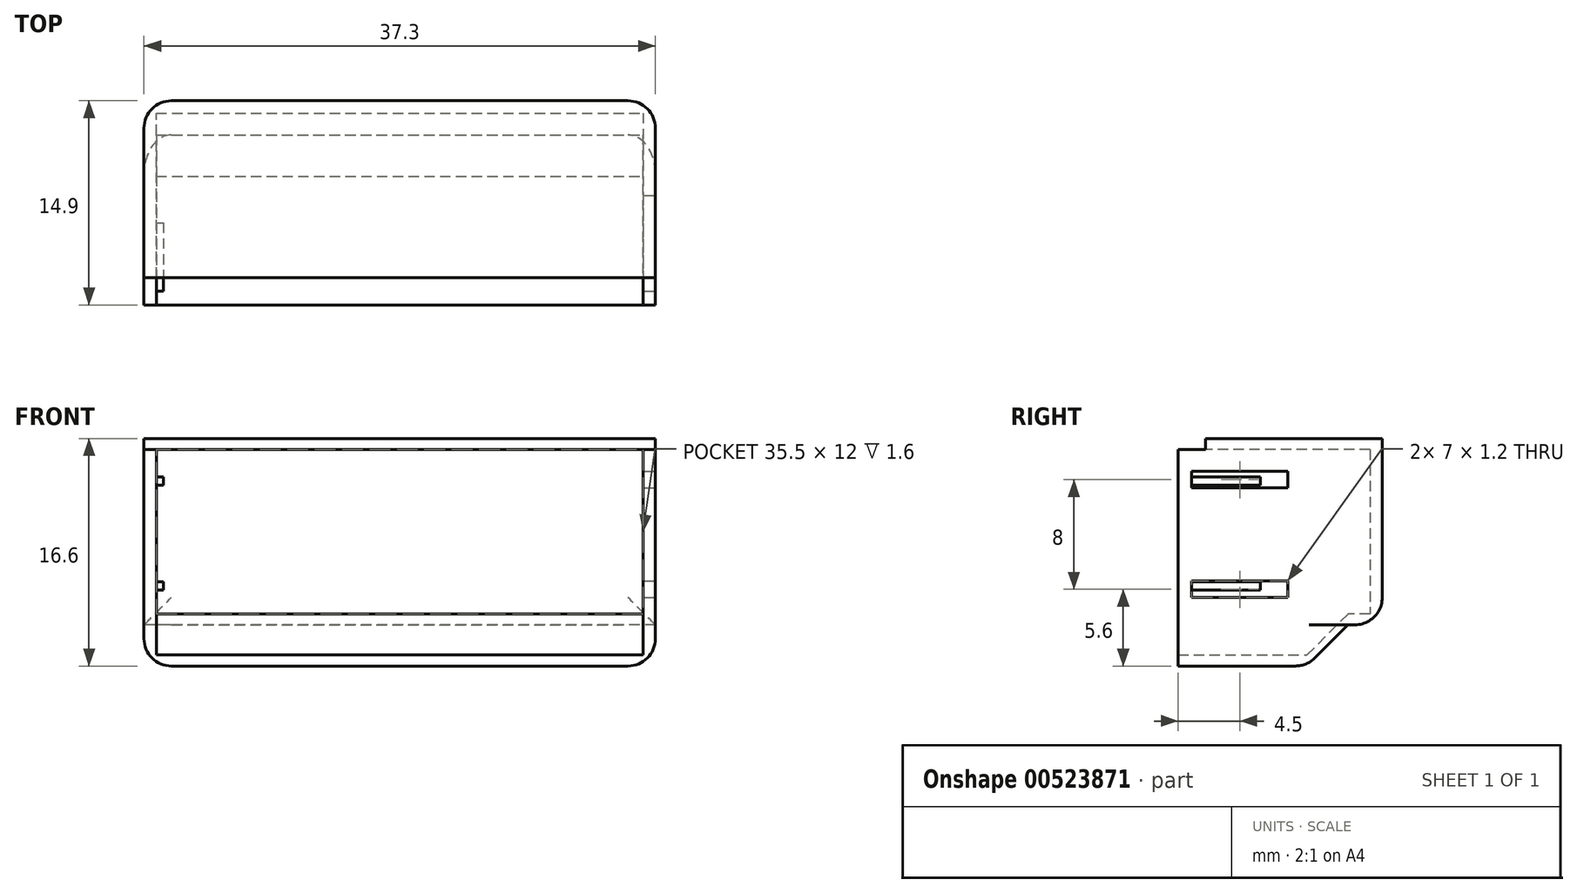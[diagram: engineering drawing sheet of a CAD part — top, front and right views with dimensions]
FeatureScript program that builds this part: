
annotation { "Feature Type Name" : "Feature", "Feature Type Description" : "" }
export const myFeature = defineFeature(function(context is Context, id is Id, definition is map)
    precondition{}
    {
        {
            var Q0;
            Q0=qCreatedBy(makeId("Top.planeOp"),FACE);
            var sketch = newSketch(context, id + "F0", { "sketchPlane" : qUnion([Q0])});
            skLineSegment(sketch, "E0", {"start": v(0, 0) * mm, "end": v(0, 14) * mm});
            skLineSegment(sketch, "E1", {"start": v(0, 14) * mm, "end": v(35.5, 14) * mm});
            skLineSegment(sketch, "E2", {"start": v(35.5, 14) * mm, "end": v(35.5, 0) * mm});
            skLineSegment(sketch, "E3.0", {"start": v(36.4, 14.9) * mm, "end": v(36.4, 0) * mm});
            skLineSegment(sketch, "E3.1", {"start": v(-0.9, 14.9) * mm, "end": v(36.4, 14.9) * mm});
            skLineSegment(sketch, "E3.2", {"start": v(-0.9, 0) * mm, "end": v(-0.9, 14.9) * mm});
            skLineSegment(sketch, "E4", {"start": v(-0.9, 0) * mm, "end": v(0, 0) * mm});
            skLineSegment(sketch, "E5", {"start": v(35.5, 0) * mm, "end": v(36.4, 0) * mm});
            skSolve(sketch);
        }
        {
            var Q0;
            Q0 = qSketchRegion(id + "F0", true);
            extrude(context, id + "F1", {"entities" : qUnion([Q0]), "depth" : 17 * mm, "offsetDistance" : 25 * mm});
        }
        {
            var Q0;
            Q0=makeQuery(id+"F1.opExtrude","SWEPT_FACE",FACE,{"disambiguationData":[OSD([sQuery(id+"F0.wireOp",EDGE,"E4")])]});
            cPlane(context, id + "F2", {"entities" : qUnion([Q0]), "cplaneType" : CPlaneType.OFFSET, "offset" : 1 * mm, "oppositeDirection" : true, "width" : 150 * mm, "height" : 150 * mm});
        }
        {
            var Q0;
            Q0=qCreatedBy(id+"F2.planeOp",FACE);
            var sketch = newSketch(context, id + "F3", { "sketchPlane" : qUnion([Q0])});
            skLineSegment(sketch, "E6.bottom", {"start": v(0, 15) * mm, "end": v(0.5, 15) * mm});
            skLineSegment(sketch, "E6.top", {"start": v(0, 14.4) * mm, "end": v(0.5, 14.4) * mm});
            skLineSegment(sketch, "E6.left", {"start": v(0, 15) * mm, "end": v(0, 14.4) * mm});
            skLineSegment(sketch, "E6.right", {"start": v(0.5, 15) * mm, "end": v(0.5, 14.4) * mm});
            skLineSegment(sketch, "E7.bottom", {"start": v(0, 6.75) * mm, "end": v(0.5, 6.75) * mm});
            skLineSegment(sketch, "E7.top", {"start": v(0, 7.35) * mm, "end": v(0.5, 7.35) * mm});
            skLineSegment(sketch, "E7.left", {"start": v(0, 7.35) * mm, "end": v(0, 6.75) * mm});
            skLineSegment(sketch, "E7.right", {"start": v(0.5, 7.35) * mm, "end": v(0.5, 6.75) * mm});
            skLineSegment(sketch, "E8.bottom", {"start": v(35.5, 15.4) * mm, "end": v(36.5, 15.4) * mm});
            skLineSegment(sketch, "E8.top", {"start": v(35.5, 14.2) * mm, "end": v(36.5, 14.2) * mm});
            skLineSegment(sketch, "E8.left", {"start": v(35.5, 15.4) * mm, "end": v(35.5, 14.2) * mm});
            skLineSegment(sketch, "E8.right", {"start": v(36.5, 15.4) * mm, "end": v(36.5, 14.2) * mm});
            skLineSegment(sketch, "E9.bottom", {"start": v(35.5, 7.4) * mm, "end": v(36.5, 7.4) * mm});
            skLineSegment(sketch, "E9.top", {"start": v(35.5, 6.2) * mm, "end": v(36.5, 6.2) * mm});
            skLineSegment(sketch, "E9.left", {"start": v(35.5, 7.4) * mm, "end": v(35.5, 6.2) * mm});
            skLineSegment(sketch, "E9.right", {"start": v(36.5, 7.4) * mm, "end": v(36.5, 6.2) * mm});
            skSolve(sketch);
        }
        {
            var Q0;
            Q0=makeQuery(id+"F3.imprint","IMPRINT",FACE,{"disambiguationData":[TD([[makeQuery(id+"F3.imprint","IMPRINT",EDGE,{"derivedFrom":sQuery(id+"F3.wireOp",EDGE,"E6.bottom")}),-1.0]])]});
            var Q1;
            Q1=makeQuery(id+"F3.imprint","IMPRINT",FACE,{"disambiguationData":[TD([[makeQuery(id+"F3.imprint","IMPRINT",EDGE,{"derivedFrom":sQuery(id+"F3.wireOp",EDGE,"E7.bottom")}),1.0]])]});
            extrude(context, id + "F4", {"entities" : qUnion([Q0, Q1]), "operationType" : NewBodyOperationType.ADD, "oppositeDirection" : true, "depth" : 5 * mm, "offsetDistance" : 25 * mm});
        }
        {
            var Q0;
            Q0=makeQuery(id+"F3.imprint","IMPRINT",FACE,{"disambiguationData":[TD([[makeQuery(id+"F3.imprint","IMPRINT",EDGE,{"derivedFrom":sQuery(id+"F3.wireOp",EDGE,"E8.bottom")}),-1.0]])]});
            var Q1;
            Q1=makeQuery(id+"F3.imprint","IMPRINT",FACE,{"disambiguationData":[TD([[makeQuery(id+"F3.imprint","IMPRINT",EDGE,{"derivedFrom":sQuery(id+"F3.wireOp",EDGE,"E9.bottom")}),-1.0]])]});
            extrude(context, id + "F5", {"entities" : qUnion([Q0, Q1]), "operationType" : NewBodyOperationType.REMOVE, "oppositeDirection" : true, "depth" : 7 * mm, "offsetDistance" : 25 * mm});
        }
        {
            var Q0;
            Q0=makeQuery(id+"F1.opExtrude","CAP_FACE",FACE,{"disambiguationData":[OSD([sQuery(id+"F0.wireOp",EDGE,"E0"),sQuery(id+"F0.wireOp",EDGE,"E1"),sQuery(id+"F0.wireOp",EDGE,"E2"),sQuery(id+"F0.wireOp",EDGE,"E3.0"),sQuery(id+"F0.wireOp",EDGE,"E3.1"),sQuery(id+"F0.wireOp",EDGE,"E3.2"),sQuery(id+"F0.wireOp",EDGE,"E4"),sQuery(id+"F0.wireOp",EDGE,"E5")])],"isStart":false});
            var sketch = newSketch(context, id + "F6", { "sketchPlane" : qUnion([Q0])});
            skLineSegment(sketch, "E10.bottom", {"start": v(36.4, 14.9) * mm, "end": v(-0.9, 14.9) * mm});
            skLineSegment(sketch, "E10.top", {"start": v(36.4, 2) * mm, "end": v(-0.9, 2) * mm});
            skLineSegment(sketch, "E10.left", {"start": v(36.4, 14.9) * mm, "end": v(36.4, 2) * mm});
            skLineSegment(sketch, "E10.right", {"start": v(-0.9, 14.9) * mm, "end": v(-0.9, 2) * mm});
            skSolve(sketch);
        }
        {
            var Q0;
            Q0=makeQuery(id+"F1.opExtrude","SWEPT_FACE",FACE,{"disambiguationData":[OSD([sQuery(id+"F0.wireOp",EDGE,"E3.0")])]});
            var sketch = newSketch(context, id + "F7", { "sketchPlane" : qUnion([Q0])});
            skLineSegment(sketch, "E11.bottom", {"start": v(14.9, 5) * mm, "end": v(12.4, 5) * mm});
            skLineSegment(sketch, "E11.top", {"start": v(14.9, 4.2) * mm, "end": v(12.4, 4.2) * mm});
            skLineSegment(sketch, "E11.left", {"start": v(14.9, 5) * mm, "end": v(14.9, 4.2) * mm});
            skLineSegment(sketch, "E11.right", {"start": v(12.4, 5) * mm, "end": v(12.4, 4.2) * mm});
            skSolve(sketch);
        }
        {
            var Q0;
            Q0 = qSketchRegion(id + "F7", true);
            var Q1;
            Q1=makeQuery(id+"F1.opExtrude","SWEPT_FACE",FACE,{"disambiguationData":[OSD([sQuery(id+"F0.wireOp",EDGE,"E3.2")])]});
            extrude(context, id + "F8", {"entities" : qUnion([Q0]), "operationType" : NewBodyOperationType.ADD, "endBound" : BoundingType.UP_TO_SURFACE, "oppositeDirection" : true, "depth" : 25 * mm, "endBoundEntityFace" : qUnion([Q1]), "offsetDistance" : 25 * mm});
        }
        {
            var Q0;
            Q0 = qSketchRegion(id + "F6", true);
            extrude(context, id + "F9", {"entities" : qUnion([Q0]), "operationType" : NewBodyOperationType.ADD, "depth" : 0.8 * mm, "offsetDistance" : 25 * mm});
        }
        {
            var Q0;
            Q0=makeQuery(id+"F1.opExtrude","SWEPT_FACE",FACE,{"disambiguationData":[OSD([sQuery(id+"F0.wireOp",EDGE,"E2")])]});
            var sketch = newSketch(context, id + "F10", { "sketchPlane" : qUnion([Q0])});
            skLineSegment(sketch, "E12.bottom", {"start": v(0, 1.2) * mm, "end": v(-9.4, 1.2) * mm});
            skLineSegment(sketch, "E12.top", {"start": v(0, 2) * mm, "end": v(-9.4, 2) * mm});
            skLineSegment(sketch, "E12.left", {"start": v(0, 1.2) * mm, "end": v(0, 2) * mm});
            skLineSegment(sketch, "E12.right", {"start": v(-9.4, 1.2) * mm, "end": v(-9.4, 2) * mm});
            skLineSegment(sketch, "E13", {"start": v(-9.4, 2) * mm, "end": v(-12.4, 5) * mm});
            skLineSegment(sketch, "E14", {"start": v(-12.4, 5) * mm, "end": v(-12.4, 4.2) * mm});
            skLineSegment(sketch, "E15", {"start": v(-12.4, 4.2) * mm, "end": v(-9.4, 1.2) * mm});
            skSolve(sketch);
        }
        {
            var Q0;
            Q0 = qSketchRegion(id + "F10", true);
            var Q1;
            Q1=makeQuery(id+"F9.boolean.opBoolean","MERGE",FACE,{"derivedFrom":[makeQuery(id+"F1.opExtrude","SWEPT_FACE",FACE,{"disambiguationData":[OSD([sQuery(id+"F0.wireOp",EDGE,"E3.2")])]}),makeQuery(id+"F9.opExtrude","SWEPT_FACE",FACE,{"disambiguationData":[OSD([sQuery(id+"F6.wireOp",EDGE,"E10.right")])]})]});
            extrude(context, id + "F11", {"entities" : qUnion([Q0]), "operationType" : NewBodyOperationType.ADD, "endBound" : BoundingType.UP_TO_SURFACE, "depth" : 25 * mm, "endBoundEntityFace" : qUnion([Q1]), "offsetDistance" : 25 * mm});
        }
        {
            var Q0;
            {var subQ3=sQuery(id+"F0.wireOp",EDGE,"E2");Q0=makeQuery(id+"F11.boolean.opBoolean","SPLIT",FACE,{"disambiguationData":[TD([makeQuery(id+"F8.opExtrude","SWEPT_FACE",FACE,{"disambiguationData":[OSD([sQuery(id+"F7.wireOp",EDGE,"E11.top")])]})])],"derivedFrom":makeQuery(id+"F1.opExtrude","SWEPT_FACE",FACE,{"disambiguationData":[OSD([subQ3])]})});}
            extrude(context, id + "F12", {"entities" : qUnion([Q0]), "operationType" : NewBodyOperationType.REMOVE, "oppositeDirection" : true, "depth" : 25 * mm, "offsetDistance" : 25 * mm, "hasSecondDirection" : true, "secondDirectionBound" : SecondDirectionBoundingType.THROUGH_ALL, "secondDirectionOppositeDirection" : false, "secondDirectionDepth" : 25 * mm});
        }
        {
            var Q0;
            {var subQ0=sQuery(id+"F0.wireOp",EDGE,"E2");var subQ1=sQuery(id+"F0.wireOp",EDGE,"E1");Q0=makeQuery(id+"F12.boolean.opBoolean","MERGE",FACE,{"derivedFrom":[makeQuery(id+"F8.boolean.opBoolean","SPLIT",FACE,{"disambiguationData":[TD([makeQuery(id+"F8.opExtrude","SWEPT_FACE",FACE,{"disambiguationData":[OSD([sQuery(id+"F7.wireOp",EDGE,"E11.top")])]})])],"derivedFrom":makeQuery(id+"F1.opExtrude","SWEPT_FACE",FACE,{"disambiguationData":[OSD([subQ1])]})}),makeQuery(id+"F12.opExtrude","SWEPT_FACE",FACE,{"disambiguationData":[OSD([subQ1,subQ0])]})]});}
            extrude(context, id + "F13", {"entities" : qUnion([Q0]), "operationType" : NewBodyOperationType.REMOVE, "endBound" : BoundingType.THROUGH_ALL, "oppositeDirection" : true, "depth" : 25 * mm, "offsetDistance" : 25 * mm});
        }
        {
            var Q0;
            Q0=makeQuery(id+"F13.boolean.opBoolean","INTERSECT",EDGE,{"derivedFrom":[makeQuery(id+"F9.boolean.opBoolean","MERGE",FACE,{"derivedFrom":[makeQuery(id+"F1.opExtrude","SWEPT_FACE",FACE,{"disambiguationData":[OSD([sQuery(id+"F0.wireOp",EDGE,"E3.1")])]}),makeQuery(id+"F9.opExtrude","SWEPT_FACE",FACE,{"disambiguationData":[OSD([sQuery(id+"F6.wireOp",EDGE,"E10.bottom")])]})]}),makeQuery(id+"F13.opExtrude","SWEPT_FACE",FACE,{"disambiguationData":[OSD([sQuery(id+"F0.wireOp",EDGE,"E1"),sQuery(id+"F0.wireOp",EDGE,"E2"),sQuery(id+"F7.wireOp",EDGE,"E11.top")])]})]});
            var Q1;
            {var subQ0=sQuery(id+"F10.wireOp",EDGE,"E15");var subQ1=sQuery(id+"F10.wireOp",EDGE,"E12.right");var subQ2=sQuery(id+"F10.wireOp",EDGE,"E12.bottom");Q1=makeQuery(id+"F12.boolean.opBoolean","MERGE",EDGE,{"derivedFrom":[makeQuery(id+"F11.opExtrude","SWEPT_EDGE",EDGE,{"disambiguationData":[OSD([subQ2,subQ1,subQ0])]}),makeQuery(id+"F12.opExtrude","SWEPT_EDGE",EDGE,{"disambiguationData":[OSD([subQ2,subQ1,subQ0])]})]});}
            var Q2;
            Q2=makeQuery(id+"F12.boolean.opBoolean","INTERSECT",EDGE,{"derivedFrom":[makeQuery(id+"F9.boolean.opBoolean","MERGE",FACE,{"derivedFrom":[makeQuery(id+"F1.opExtrude","SWEPT_FACE",FACE,{"disambiguationData":[OSD([sQuery(id+"F0.wireOp",EDGE,"E3.2")])]}),makeQuery(id+"F9.opExtrude","SWEPT_FACE",FACE,{"disambiguationData":[OSD([sQuery(id+"F6.wireOp",EDGE,"E10.right")])]})]}),makeQuery(id+"F12.opExtrude","SWEPT_FACE",FACE,{"disambiguationData":[OSD([sQuery(id+"F10.wireOp",EDGE,"E12.bottom")])]})]});
            var Q3;
            Q3=makeQuery(id+"F12.boolean.opBoolean","INTERSECT",EDGE,{"derivedFrom":[makeQuery(id+"F9.boolean.opBoolean","MERGE",FACE,{"derivedFrom":[makeQuery(id+"F1.opExtrude","SWEPT_FACE",FACE,{"disambiguationData":[OSD([sQuery(id+"F0.wireOp",EDGE,"E3.0")])]}),makeQuery(id+"F9.opExtrude","SWEPT_FACE",FACE,{"disambiguationData":[OSD([sQuery(id+"F6.wireOp",EDGE,"E10.left")])]})]}),makeQuery(id+"F12.opExtrude","SWEPT_FACE",FACE,{"disambiguationData":[OSD([sQuery(id+"F10.wireOp",EDGE,"E12.bottom")])]})]});
            var Q4;
            Q4=makeQuery(id+"F12.boolean.opBoolean","INTERSECT",EDGE,{"derivedFrom":[makeQuery(id+"F9.boolean.opBoolean","MERGE",FACE,{"derivedFrom":[makeQuery(id+"F1.opExtrude","SWEPT_FACE",FACE,{"disambiguationData":[OSD([sQuery(id+"F0.wireOp",EDGE,"E3.2")])]}),makeQuery(id+"F9.opExtrude","SWEPT_FACE",FACE,{"disambiguationData":[OSD([sQuery(id+"F6.wireOp",EDGE,"E10.right")])]})]}),makeQuery(id+"F12.opExtrude","SWEPT_FACE",FACE,{"disambiguationData":[OSD([sQuery(id+"F10.wireOp",EDGE,"E15")])]})]});
            var Q5;
            Q5=makeQuery(id+"F12.boolean.opBoolean","INTERSECT",EDGE,{"derivedFrom":[makeQuery(id+"F9.boolean.opBoolean","MERGE",FACE,{"derivedFrom":[makeQuery(id+"F1.opExtrude","SWEPT_FACE",FACE,{"disambiguationData":[OSD([sQuery(id+"F0.wireOp",EDGE,"E3.0")])]}),makeQuery(id+"F9.opExtrude","SWEPT_FACE",FACE,{"disambiguationData":[OSD([sQuery(id+"F6.wireOp",EDGE,"E10.left")])]})]}),makeQuery(id+"F12.opExtrude","SWEPT_FACE",FACE,{"disambiguationData":[OSD([sQuery(id+"F10.wireOp",EDGE,"E15")])]})]});
            var Q6;
            Q6=makeQuery(id+"F9.boolean.opBoolean","MERGE",EDGE,{"derivedFrom":[makeQuery(id+"F1.opExtrude","SWEPT_EDGE",EDGE,{"disambiguationData":[OSD([sQuery(id+"F0.wireOp",EDGE,"E3.0"),sQuery(id+"F0.wireOp",EDGE,"E3.1")])]}),makeQuery(id+"F9.opExtrude","SWEPT_EDGE",EDGE,{"disambiguationData":[OSD([sQuery(id+"F6.wireOp",EDGE,"E10.bottom"),sQuery(id+"F6.wireOp",EDGE,"E10.left")])]})]});
            var Q7;
            Q7=makeQuery(id+"F9.boolean.opBoolean","MERGE",EDGE,{"derivedFrom":[makeQuery(id+"F1.opExtrude","SWEPT_EDGE",EDGE,{"disambiguationData":[OSD([sQuery(id+"F0.wireOp",EDGE,"E3.1"),sQuery(id+"F0.wireOp",EDGE,"E3.2")])]}),makeQuery(id+"F9.opExtrude","SWEPT_EDGE",EDGE,{"disambiguationData":[OSD([sQuery(id+"F6.wireOp",EDGE,"E10.bottom"),sQuery(id+"F6.wireOp",EDGE,"E10.right")])]})]});
            var Q8;
            {var subQ0=sQuery(id+"F7.wireOp",EDGE,"E11.top");var subQ1=sQuery(id+"F6.wireOp",EDGE,"E10.left");var subQ2=sQuery(id+"F0.wireOp",EDGE,"E3.0");var subQ3=sQuery(id+"F0.wireOp",EDGE,"E2");Q8=makeQuery(id+"F13.boolean.opBoolean","MERGE",EDGE,{"derivedFrom":[makeQuery(id+"F12.boolean.opBoolean","INTERSECT",EDGE,{"derivedFrom":[makeQuery(id+"F9.boolean.opBoolean","MERGE",FACE,{"derivedFrom":[makeQuery(id+"F1.opExtrude","SWEPT_FACE",FACE,{"disambiguationData":[OSD([subQ2])]}),makeQuery(id+"F9.opExtrude","SWEPT_FACE",FACE,{"disambiguationData":[OSD([subQ1])]})]}),makeQuery(id+"F12.opExtrude","SWEPT_FACE",FACE,{"disambiguationData":[OSD([subQ3,subQ0])]})]}),makeQuery(id+"F13.opExtrude","SWEPT_EDGE",EDGE,{"disambiguationData":[OSD([sQuery(id+"F0.wireOp",EDGE,"E1"),subQ3,subQ2,subQ1,subQ0])]})]});}
            var Q9;
            {var subQ0=sQuery(id+"F7.wireOp",EDGE,"E11.top");var subQ1=sQuery(id+"F6.wireOp",EDGE,"E10.right");var subQ2=sQuery(id+"F0.wireOp",EDGE,"E3.2");var subQ3=sQuery(id+"F0.wireOp",EDGE,"E2");Q9=makeQuery(id+"F13.boolean.opBoolean","MERGE",EDGE,{"derivedFrom":[makeQuery(id+"F12.boolean.opBoolean","INTERSECT",EDGE,{"derivedFrom":[makeQuery(id+"F9.boolean.opBoolean","MERGE",FACE,{"derivedFrom":[makeQuery(id+"F1.opExtrude","SWEPT_FACE",FACE,{"disambiguationData":[OSD([subQ2])]}),makeQuery(id+"F9.opExtrude","SWEPT_FACE",FACE,{"disambiguationData":[OSD([subQ1])]})]}),makeQuery(id+"F12.opExtrude","SWEPT_FACE",FACE,{"disambiguationData":[OSD([subQ3,subQ0])]})]}),makeQuery(id+"F13.opExtrude","SWEPT_EDGE",EDGE,{"disambiguationData":[OSD([sQuery(id+"F0.wireOp",EDGE,"E1"),subQ3,subQ2,subQ1,subQ0])]})]});}
            fillet(context, id + "F14", {"entities" : qUnion([Q0, Q1, Q2, Q3, Q4, Q5, Q6, Q7, Q8, Q9]), "radius" : 2 * mm, "tangentPropagation" : true, "allowEdgeOverflow" : false});
        }
    });
